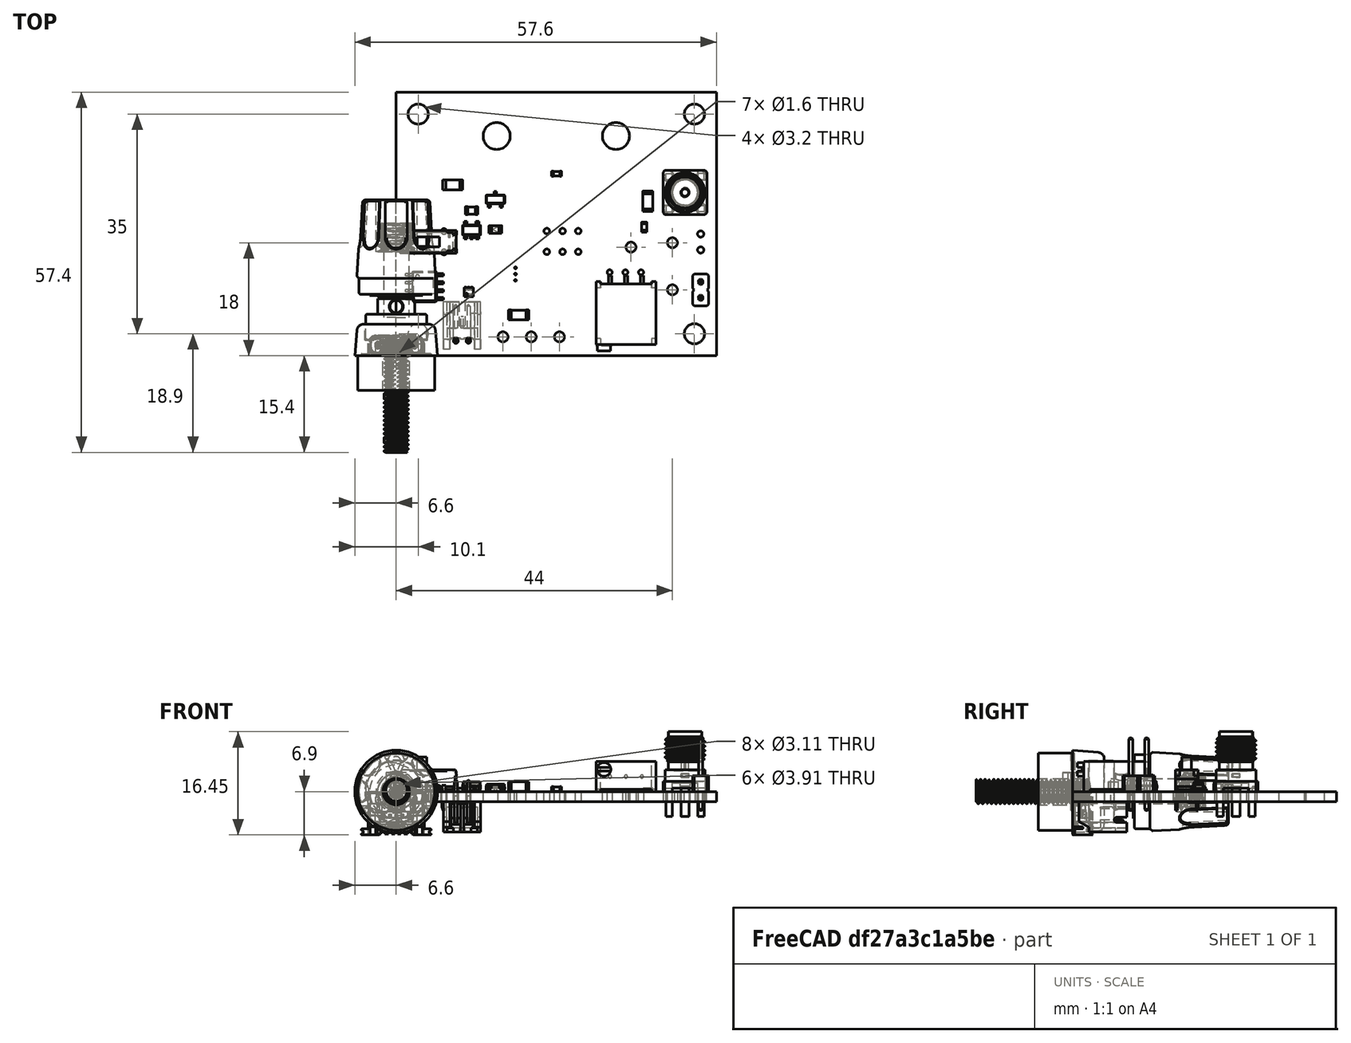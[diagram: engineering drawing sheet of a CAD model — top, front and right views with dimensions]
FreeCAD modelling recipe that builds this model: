
FCSTD DOCUMENT  (FreeCAD 0.20R29603 (Git))
Label: SCuSA_RevA1_PCBA
License: All rights reserved
LicenseURL: http://en.wikipedia.org/wiki/All_rights_reserved
objects: App::Link×51, Part::Feature×39, App::Part×12, PartDesign::CoordinateSystem×1, Sketcher::SketchObject×1
note: 41 computed .brp shape members not serialized (recipe doc carries the construction recipe); baked Part::Feature solids carry a one-line shape summary decoded from their .brp

FEATURE [PartDesign::CoordinateSystem] Local_CS_3e51
  AttacherType = Attacher::AttachEngine3D
  MapMode = 2
  Support = -> [X_Axis001]
FEATURE [Part::Feature] Pcb_3e51
  Placement = pos=(-112,104,0) rot=(0,0,1;0rad)
  shape: bbox 51 x 42 x 1.6 mm, 47 faces (baked)
FEATURE [Sketcher::SketchObject] PCB_Sketch_3e51
  FullyConstrained = false
  sketch-geometry (4):
    g0: LineSegment StartX=51 StartY=0 StartZ=0 EndX=0 EndY=0 EndZ=0
    g1: LineSegment StartX=0 StartY=42 StartZ=0 EndX=51 EndY=42 EndZ=0
    g2: LineSegment StartX=0 StartY=0 StartZ=0 EndX=0 EndY=42 EndZ=0
    g3: LineSegment StartX=51 StartY=42 StartZ=0 EndX=51 EndY=0 EndZ=0
  constraints (4):
    c: Coincident(g0,g2)
    c: Coincident(g1,g2)
    c: Coincident(g0,g3)
    c: Coincident(g1,g3)
FEATURE [App::Part] Board_Geoms_3e51
  Group = -> [Pcb_3e51,PCB_Sketch_3e51]
  Origin = -> Origin
FEATURE [Part::Feature] Shape  label="R118_R_1206_3216Metric_9a429e010c18"
  Placement = pos=(40.05,24.6,0) rot=(0,0,1;1.5708rad)
  shape: bbox 1.6 x 3.2 x 0.55 mm, 26 faces (baked)
FEATURE [Part::Feature] Shape001  label="C110_C_0603_1608Metric_07e89f88e059"
  Placement = pos=(25.55,29,0) rot=(0,0,1;3.14159rad)
  shape: bbox 1.6 x 0.8 x 0.8 mm, 28 faces (baked)
FEATURE [Part::Feature] Shape002  label="R121_R_0603_1608Metric_cabd63930a75"
  Placement = pos=(39.5,20.5,0) rot=(0,0,-1;1.5708rad)
  shape: bbox 0.8 x 1.6 x 0.45 mm, 26 faces (baked)
FEATURE [Part::Feature] Shape003  label="F101_Fuse_1206_3216Metric_160eb9ee9b08"
  Placement = pos=(9,27.2,0) rot=(0,0,1;0rad)
  shape: bbox 3.2 x 1.6 x 0.55 mm, 26 faces (baked)
FEATURE [Part::Feature] Shape004  label="J108_PinHeader_1x02_P254mm_Vertical_696c06d13264"
  Placement = pos=(48.5,9.225,0) rot=(0,0,1;3.14159rad)
  shape: bbox 2.54 x 5.08 x 11.54 mm, 52 faces (baked)
FEATURE [Part::Feature] Shape005  label="C101_C_0805_2012Metric_832099bd49ec"
  Placement = pos=(12,23.1,0) rot=(0,0,1;3.14159rad)
  shape: bbox 2 x 1.25 x 1.25 mm, 28 faces (baked)
FEATURE [App::Link] R121_R_0603_1608Metric_cabd63930a75_ln_  label="R103_R_0603_1608Metric_e52815511993"
  LinkPlacement = pos=(8.4,22.9,0) rot=(0,0,1;3.14159rad)
  LinkedObject = -> Shape002
  Placement = pos=(8.4,22.9,0) rot=(0,0,1;3.14159rad)
FEATURE [App::Link] C110_C_0603_1608Metric_07e89f88e059_ln_  label="C114_C_0603_1608Metric_c5f3be501f81"
  LinkPlacement = pos=(23.2,9.4,0) rot=(0,0,1;1.5708rad)
  LinkedObject = -> Shape001
  Placement = pos=(23.2,9.4,0) rot=(0,0,1;1.5708rad)
FEATURE [Part::Feature] Part__Feature  label="WSON-12 v7"
  shape: bbox 1 x 0.25 x 2.65 mm, 7 faces (baked)
FEATURE [Part::Feature] Part__Feature001  label="WSON-12 v008"
  shape: bbox 0.35 x 0.25 x 0.25 mm, 6 faces (baked)
FEATURE [Part::Feature] Part__Feature002  label="WSON-12 v009"
  shape: bbox 0.35 x 0.25 x 0.25 mm, 6 faces (baked)
FEATURE [Part::Feature] Part__Feature003  label="WSON-12 v010"
  shape: bbox 0.35 x 0.25 x 0.25 mm, 6 faces (baked)
FEATURE [Part::Feature] Part__Feature004  label="WSON-12 v011"
  shape: bbox 0.35 x 0.25 x 0.25 mm, 6 faces (baked)
FEATURE [Part::Feature] Part__Feature005  label="WSON-12 v012"
  shape: bbox 0.35 x 0.25 x 0.25 mm, 6 faces (baked)
FEATURE [Part::Feature] Part__Feature006  label="WSON-12 v013"
  shape: bbox 0.35 x 0.25 x 0.25 mm, 6 faces (baked)
FEATURE [Part::Feature] Part__Feature007  label="WSON-12 v014"
  shape: bbox 0.35 x 0.25 x 0.25 mm, 6 faces (baked)
FEATURE [Part::Feature] Part__Feature008  label="WSON-12 v015"
  shape: bbox 0.35 x 0.25 x 0.25 mm, 6 faces (baked)
FEATURE [Part::Feature] Part__Feature009  label="WSON-12 v016"
  shape: bbox 0.35 x 0.25 x 0.25 mm, 6 faces (baked)
FEATURE [Part::Feature] Part__Feature010  label="WSON-12 v017"
  shape: bbox 0.35 x 0.25 x 0.25 mm, 6 faces (baked)
FEATURE [Part::Feature] Part__Feature011  label="WSON-12 v018"
  shape: bbox 0.35 x 0.25 x 0.25 mm, 6 faces (baked)
FEATURE [Part::Feature] Part__Feature012  label="WSON-12 v019"
  shape: bbox 0.35 x 0.25 x 0.25 mm, 6 faces (baked)
FEATURE [Part::Feature] Part__Feature013  label="WSON-12 v020"
  shape: bbox 2.001 x 0.8006 x 3.001 mm, 603 faces (baked)
FEATURE [App::Part] WSON_12_v7  label="U104_WSON-12 v021_6ffd8b18686f"
  Group = -> [Part__Feature,Part__Feature001,Part__Feature002,Part__Feature003,Part__Feature004,Part__Feature005,Part__Feature006,Part__Feature007,Part__Feature008,Part__Feature009,Part__Feature010,Part__Feature011,Part__Feature012,Part__Feature013]
  Origin = -> Origin008
  Placement = pos=(19,13,0) rot=(1,0,0;1.5708rad)
FEATURE [Part::Feature] Part__Feature014  label="TestPoint_Loop_D2_60mm_Drill1_6mm_Beaded_cp"
  shape: bbox 3.2 x 3.2 x 3 mm, 4 faces (baked)
FEATURE [Part::Feature] Part__Feature015  label="TestPoint_Loop_D2_60mm_Drill1_6mm_Beaded_cp001"
  shape: bbox 3.649 x 1.14 x 9.307 mm, 7 faces (baked)
FEATURE [App::Part] TestPoint_Loop_D2_60mm_Drill1_6mm_Beaded_cp  label="TP106_TestPoint_Loop_D2_60mm_Drill1_6mm_Beaded_cp002_0780feeba4dd"
  Group = -> [Part__Feature014,Part__Feature015]
  Origin = -> Origin009
  Placement = pos=(37.4,17.3,0) rot=(0,0,1;1.5708rad)
FEATURE [App::Link] R121_R_0603_1608Metric_cabd63930a75_ln_001  label="R105_R_0603_1608Metric_8828eca0330c"
  LinkPlacement = pos=(12.2,13.75,0) rot=(0,0,1;3.14159rad)
  LinkedObject = -> Shape002
  Placement = pos=(12.2,13.75,0) rot=(0,0,1;3.14159rad)
FEATURE [App::Link] C101_C_0805_2012Metric_832099bd49ec_ln_  label="C102_C_0805_2012Metric_9881d72c0956"
  LinkPlacement = pos=(11.9,16.9,0) rot=(0,0,1;3.14159rad)
  LinkedObject = -> Shape005
  Placement = pos=(11.9,16.9,0) rot=(0,0,1;3.14159rad)
FEATURE [App::Link] C110_C_0603_1608Metric_07e89f88e059_ln_001  label="C111_C_0603_1608Metric_e0c0d5fa783b"
  LinkPlacement = pos=(22.2,29,0) rot=(0,0,1;3.14159rad)
  LinkedObject = -> Shape001
  Placement = pos=(22.2,29,0) rot=(0,0,1;3.14159rad)
FEATURE [App::Link] R121_R_0603_1608Metric_cabd63930a75_ln_002  label="R113_R_0603_1608Metric_61fe00350bf9"
  LinkPlacement = pos=(19.05,8.5,0) rot=(0,0,1;3.14159rad)
  LinkedObject = -> Shape002
  Placement = pos=(19.05,8.5,0) rot=(0,0,1;3.14159rad)
FEATURE [App::Link] C110_C_0603_1608Metric_07e89f88e059_ln_002  label="C106_C_0603_1608Metric_96d47e7760c2"
  LinkPlacement = pos=(21.55,13,0) rot=(0,0,-1;1.5708rad)
  LinkedObject = -> Shape001
  Placement = pos=(21.55,13,0) rot=(0,0,-1;1.5708rad)
FEATURE [App::Link] C110_C_0603_1608Metric_07e89f88e059_ln_003  label="C109_C_0603_1608Metric_a759c64c54e8"
  LinkPlacement = pos=(28.9,29,0) rot=(0,0,1;3.14159rad)
  LinkedObject = -> Shape001
  Placement = pos=(28.9,29,0) rot=(0,0,1;3.14159rad)
FEATURE [App::Link] C110_C_0603_1608Metric_07e89f88e059_ln_004  label="C115_C_0603_1608Metric_735d576579cb"
  LinkPlacement = pos=(28.9,22,0) rot=(0,0,1;0rad)
  LinkedObject = -> Shape001
  Placement = pos=(28.9,22,0) rot=(0,0,1;0rad)
FEATURE [App::Link] TP106_TestPoint_Loop_D2_60mm_Drill1_6mm_Beaded_cp002_0780feeba4dd_ln_  label="TP102_TestPoint_Loop_D2_60mm_Drill1_6mm_Beaded_cp002_ab26968e4f7d"
  LinkPlacement = pos=(17,3,0) rot=(0,0,1;0rad)
  LinkedObject = -> TestPoint_Loop_D2_60mm_Drill1_6mm_Beaded_cp
  Placement = pos=(17,3,0) rot=(0,0,1;0rad)
FEATURE [App::Link] C101_C_0805_2012Metric_832099bd49ec_ln_001  label="C108_C_0805_2012Metric_e86135985600"
  LinkPlacement = pos=(16,9.25,0) rot=(0,0,-1;1.5708rad)
  LinkedObject = -> Shape005
  Placement = pos=(16,9.25,0) rot=(0,0,-1;1.5708rad)
FEATURE [Part::Feature] Shape006  label="Q101_SOIC_8_39x49mm_P127mm_18785c1fbfb3"
  Placement = pos=(4.5,11,0) rot=(0,0,1;0rad)
  shape: bbox 6 x 4.9 x 1.75 mm, 156 faces (baked)
FEATURE [App::Link] R121_R_0603_1608Metric_cabd63930a75_ln_003  label="R109_R_0603_1608Metric_f4df95fcec91"
  LinkPlacement = pos=(15.8,22.15,0) rot=(0,0,1;0rad)
  LinkedObject = -> Shape002
  Placement = pos=(15.8,22.15,0) rot=(0,0,1;0rad)
FEATURE [Part::Feature] Shape007  label="SW101_CuK_JS202011CQN_DPDT_straight_5f730d750727"
  Placement = pos=(7.6075,16.5,0) rot=(0,0,1;3.14159rad)
  shape: bbox 9 x 3.61 x 8.5 mm, 178 faces (baked)
FEATURE [App::Link] C110_C_0603_1608Metric_07e89f88e059_ln_005  label="C118_C_0603_1608Metric_af693a659c10"
  LinkPlacement = pos=(33.2,20.1,0) rot=(0,0,1;0rad)
  LinkedObject = -> Shape001
  Placement = pos=(33.2,20.1,0) rot=(0,0,1;0rad)
FEATURE [App::Link] SW101_CuK_JS202011CQN_DPDT_straight_5f730d750727_ln_  label="SW102_CuK_JS202011CQN_DPDT_straight_acea3379d2f1"
  LinkPlacement = pos=(23.9925,19.85,0) rot=(0,0,1;0rad)
  LinkedObject = -> Shape007
  Placement = pos=(23.9925,19.85,0) rot=(0,0,1;0rad)
FEATURE [App::Link] C110_C_0603_1608Metric_07e89f88e059_ln_006  label="C105_C_0603_1608Metric_287e28563a33"
  LinkPlacement = pos=(20,15.7,0) rot=(0,0,1;3.14159rad)
  LinkedObject = -> Shape001
  Placement = pos=(20,15.7,0) rot=(0,0,1;3.14159rad)
FEATURE [App::Link] TP106_TestPoint_Loop_D2_60mm_Drill1_6mm_Beaded_cp002_0780feeba4dd_ln_001  label="TP101_TestPoint_Loop_D2_60mm_Drill1_6mm_Beaded_cp002_a418f8038e49"
  LinkPlacement = pos=(21.5,3,0) rot=(0,0,1;0rad)
  LinkedObject = -> TestPoint_Loop_D2_60mm_Drill1_6mm_Beaded_cp
  Placement = pos=(21.5,3,0) rot=(0,0,1;0rad)
FEATURE [Part::Feature] Shape008  label="FB101_L_1206_3216Metric_6ecc6a01b1a7"
  Placement = pos=(19.5,6.5,0) rot=(0,0,1;0rad)
  shape: bbox 3.2 x 1.6 x 1.6 mm, 28 faces (baked)
FEATURE [App::Link] C110_C_0603_1608Metric_07e89f88e059_ln_007  label="C117_C_0603_1608Metric_b9cc278da1dd"
  LinkPlacement = pos=(33.25,27.1,0) rot=(0,0,1;0rad)
  LinkedObject = -> Shape001
  Placement = pos=(33.25,27.1,0) rot=(0,0,1;0rad)
FEATURE [Part::Feature] Shape009  label="J105_60312002114503_f594866c6ba6"
  Placement = pos=(46,26,1.65) rot=(1,0,0;3.14159rad)
  shape: bbox 7.319 x 7.009 x 13.51 mm, 77 faces (baked)
FEATURE [App::Link] C110_C_0603_1608Metric_07e89f88e059_ln_008  label="C116_C_0603_1608Metric_dd78862adcb4"
  LinkPlacement = pos=(20.7,25.2,0) rot=(0,0,1;1.5708rad)
  LinkedObject = -> Shape001
  Placement = pos=(20.7,25.2,0) rot=(0,0,1;1.5708rad)
FEATURE [App::Link] C110_C_0603_1608Metric_07e89f88e059_ln_009  label="C104_C_0603_1608Metric_8d6246460c0c"
  LinkPlacement = pos=(16.5,13,0) rot=(0,0,-1;1.5708rad)
  LinkedObject = -> Shape001
  Placement = pos=(16.5,13,0) rot=(0,0,-1;1.5708rad)
FEATURE [App::Link] R121_R_0603_1608Metric_cabd63930a75_ln_004  label="R115_R_0603_1608Metric_e91c1c194d21"
  LinkPlacement = pos=(26.3,31.5,0) rot=(0,0,-1;1.5708rad)
  LinkedObject = -> Shape002
  Placement = pos=(26.3,31.5,0) rot=(0,0,-1;1.5708rad)
FEATURE [Part::Feature] Part__Feature016  label="USB4135-GF-A"
  shape: bbox 11.15 x 3.257 x 6.907 mm, 318 faces (baked)
FEATURE [Part::Feature] Part__Feature017  label="USB4135-GF-A001"
  shape: bbox 8.3 x 2.985 x 6.55 mm, 467 faces (baked)
FEATURE [App::Part] USB4135_GF_A  label="J101_USB4135-GF-A002_08b6693a03fd"
  Group = -> [Part__Feature016,Part__Feature017]
  Origin = -> Origin010
  Placement = pos=(-1.5175,29.25,0) rot=(0.57735,-0.57735,-0.57735;2.0944rad)
FEATURE [App::Link] FB101_L_1206_3216Metric_6ecc6a01b1a7_ln_  label="FB100_L_1206_3216Metric_5c9160750dc1"
  LinkPlacement = pos=(26.5,13.5,0) rot=(0,0,1;0rad)
  LinkedObject = -> Shape008
  Placement = pos=(26.5,13.5,0) rot=(0,0,1;0rad)
FEATURE [App::Link] R121_R_0603_1608Metric_cabd63930a75_ln_005  label="R112_R_0603_1608Metric_1715ab4cdc12"
  LinkPlacement = pos=(21.65,9.4,0) rot=(0,0,-1;1.5708rad)
  LinkedObject = -> Shape002
  Placement = pos=(21.65,9.4,0) rot=(0,0,-1;1.5708rad)
FEATURE [App::Link] TP106_TestPoint_Loop_D2_60mm_Drill1_6mm_Beaded_cp002_0780feeba4dd_ln_002  label="TP104_TestPoint_Loop_D2_60mm_Drill1_6mm_Beaded_cp002_50bb3ab2e26f"
  LinkPlacement = pos=(26,3,0) rot=(0,0,1;0rad)
  LinkedObject = -> TestPoint_Loop_D2_60mm_Drill1_6mm_Beaded_cp
  Placement = pos=(26,3,0) rot=(0,0,1;0rad)
FEATURE [App::Link] R118_R_1206_3216Metric_9a429e010c18_ln_  label="R114_R_1206_3216Metric_9449b8210d6c"
  LinkPlacement = pos=(25.5,34.35,0) rot=(0,0,1;3.14159rad)
  LinkedObject = -> Shape
  Placement = pos=(25.5,34.35,0) rot=(0,0,1;3.14159rad)
FEATURE [App::Link] C110_C_0603_1608Metric_07e89f88e059_ln_010  label="C107_C_0603_1608Metric_1132f46c80d0"
  LinkPlacement = pos=(19.05,10.25,0) rot=(0,0,1;0rad)
  LinkedObject = -> Shape001
  Placement = pos=(19.05,10.25,0) rot=(0,0,1;0rad)
FEATURE [App::Link] R121_R_0603_1608Metric_cabd63930a75_ln_006  label="R102_R_0603_1608Metric_428a7ca26184"
  LinkPlacement = pos=(8.2,29.15,0) rot=(0,0,1;0rad)
  LinkedObject = -> Shape002
  Placement = pos=(8.2,29.15,0) rot=(0,0,1;0rad)
FEATURE [App::Link] C110_C_0603_1608Metric_07e89f88e059_ln_011  label="C113_C_0603_1608Metric_c568501282b4"
  LinkPlacement = pos=(36.6,27.1,0) rot=(0,0,1;0rad)
  LinkedObject = -> Shape001
  Placement = pos=(36.6,27.1,0) rot=(0,0,1;0rad)
FEATURE [App::Link] R121_R_0603_1608Metric_cabd63930a75_ln_007  label="R116_R_0603_1608Metric_7018264d671d"
  LinkPlacement = pos=(24.8,31.5,0) rot=(0,0,-1;1.5708rad)
  LinkedObject = -> Shape002
  Placement = pos=(24.8,31.5,0) rot=(0,0,-1;1.5708rad)
FEATURE [Part::Feature] Shape010  label="D102_LED_0805_2012Metric_8af6430a5faa"
  Placement = pos=(15.8,20.1,0) rot=(0,0,1;0rad)
  shape: bbox 2 x 1.25 x 1.1 mm, 50 faces (baked)
FEATURE [App::Link] D102_LED_0805_2012Metric_8af6430a5faa_ln_  label="D103_LED_0805_2012Metric_5064c74abf3b"
  LinkPlacement = pos=(15.8,17.9,0) rot=(0,0,1;3.14159rad)
  LinkedObject = -> Shape010
  Placement = pos=(15.8,17.9,0) rot=(0,0,1;3.14159rad)
FEATURE [App::Link] C110_C_0603_1608Metric_07e89f88e059_ln_012  label="C112_C_0603_1608Metric_2f680c3bccde"
  LinkPlacement = pos=(25.55,22,0) rot=(0,0,1;3.14159rad)
  LinkedObject = -> Shape001
  Placement = pos=(25.55,22,0) rot=(0,0,1;3.14159rad)
FEATURE [App::Link] TP106_TestPoint_Loop_D2_60mm_Drill1_6mm_Beaded_cp002_0780feeba4dd_ln_003  label="TP108_TestPoint_Loop_D2_60mm_Drill1_6mm_Beaded_cp002_35738ac4b5fc"
  LinkPlacement = pos=(44,18,0) rot=(0,0,1;1.5708rad)
  LinkedObject = -> TestPoint_Loop_D2_60mm_Drill1_6mm_Beaded_cp
  Placement = pos=(44,18,0) rot=(0,0,1;1.5708rad)
FEATURE [App::Link] R121_R_0603_1608Metric_cabd63930a75_ln_008  label="R101_R_0603_1608Metric_6d1fb4459d4d"
  LinkPlacement = pos=(8.2,30.7,0) rot=(0,0,1;0rad)
  LinkedObject = -> Shape002
  Placement = pos=(8.2,30.7,0) rot=(0,0,1;0rad)
FEATURE [Part::Feature] Shape011  label="U103_SOT_23_415030393587"
  Placement = pos=(15.8,24.9,0) rot=(0,0,1;1.5708rad)
  shape: bbox 3 x 2.5 x 1.2 mm, 76 faces (baked)
FEATURE [App::Link] R121_R_0603_1608Metric_cabd63930a75_ln_009  label="R110_R_0603_1608Metric_f7e6a50cc7fa"
  LinkPlacement = pos=(20,17.25,0) rot=(0,0,1;3.14159rad)
  LinkedObject = -> Shape002
  Placement = pos=(20,17.25,0) rot=(0,0,1;3.14159rad)
FEATURE [App::Link] C110_C_0603_1608Metric_07e89f88e059_ln_013  label="C121_C_0603_1608Metric_b24aff25157a"
  LinkPlacement = pos=(41,20.5,0) rot=(0,0,1;1.5708rad)
  LinkedObject = -> Shape001
  Placement = pos=(41,20.5,0) rot=(0,0,1;1.5708rad)
FEATURE [App::Link] C110_C_0603_1608Metric_07e89f88e059_ln_014  label="C120_C_0603_1608Metric_3728ccd4f199"
  LinkPlacement = pos=(18.6,23.1375,0) rot=(0,0,1;1.5708rad)
  LinkedObject = -> Shape001
  Placement = pos=(18.6,23.1375,0) rot=(0,0,1;1.5708rad)
FEATURE [Part::Feature] Shape012  label="RV101_Cut_b268e7737479"
  Placement = pos=(41.55,22.79,6.4) rot=(0,0.707107,-0.707107;3.14159rad)
  shape: bbox 9.53 x 12.05 x 4.83 mm, 32 faces (baked)
FEATURE [App::Link] Q101_SOIC_8_39x49mm_P127mm_18785c1fbfb3_ln_  label="U105_SOIC_8_39x49mm_P127mm_81b4a2160633"
  LinkPlacement = pos=(25.55,25.5,0) rot=(0,0,1;0rad)
  LinkedObject = -> Shape006
  Placement = pos=(25.55,25.5,0) rot=(0,0,1;0rad)
FEATURE [App::Link] R121_R_0603_1608Metric_cabd63930a75_ln_010  label="R122_R_0603_1608Metric_47ff7c3b82b1"
  LinkPlacement = pos=(6.6,33.9125,0) rot=(0,0,-1;1.5708rad)
  LinkedObject = -> Shape002
  Placement = pos=(6.6,33.9125,0) rot=(0,0,-1;1.5708rad)
FEATURE [App::Link] C110_C_0603_1608Metric_07e89f88e059_ln_015  label="C103_C_0603_1608Metric_b43a54b29ec9"
  LinkPlacement = pos=(12.2,12.15,0) rot=(0,0,1;0rad)
  LinkedObject = -> Shape001
  Placement = pos=(12.2,12.15,0) rot=(0,0,1;0rad)
FEATURE [App::Link] R121_R_0603_1608Metric_cabd63930a75_ln_011  label="R104_R_0603_1608Metric_4504fa6f6234"
  LinkPlacement = pos=(12,24.9,0) rot=(0,0,1;3.14159rad)
  LinkedObject = -> Shape002
  Placement = pos=(12,24.9,0) rot=(0,0,1;3.14159rad)
FEATURE [App::Link] R121_R_0603_1608Metric_cabd63930a75_ln_012  label="R117_R_0603_1608Metric_145afd5d1bbc"
  LinkPlacement = pos=(15.75,16.05,0) rot=(0,0,1;3.14159rad)
  LinkedObject = -> Shape002
  Placement = pos=(15.75,16.05,0) rot=(0,0,1;3.14159rad)
FEATURE [App::Link] Q101_SOIC_8_39x49mm_P127mm_18785c1fbfb3_ln_001  label="U106_SOIC_8_39x49mm_P127mm_f8bf6cf0ab73"
  LinkPlacement = pos=(34.95,23.6,0) rot=(0,0,1;0rad)
  LinkedObject = -> Shape006
  Placement = pos=(34.95,23.6,0) rot=(0,0,1;0rad)
FEATURE [Part::Feature] Shape013  label="U101_SOT_23_5_b81ba866f2ca"
  Placement = pos=(12,20,0) rot=(0,0,1;1.5708rad)
  shape: bbox 2.9 x 2.8 x 1.55 mm, 109 faces (baked)
FEATURE [App::Link] R121_R_0603_1608Metric_cabd63930a75_ln_013  label="R108_R_0603_1608Metric_1a3b190c03d7"
  LinkPlacement = pos=(4.7,7.5,0) rot=(0,0,1;0rad)
  LinkedObject = -> Shape002
  Placement = pos=(4.7,7.5,0) rot=(0,0,1;0rad)
FEATURE [App::Link] R121_R_0603_1608Metric_cabd63930a75_ln_014  label="R111_R_0603_1608Metric_a0045bdc3730"
  LinkPlacement = pos=(20,18.8,0) rot=(0,0,1;0rad)
  LinkedObject = -> Shape002
  Placement = pos=(20,18.8,0) rot=(0,0,1;0rad)
FEATURE [Part::Feature] Shape014  label="U102_WSON6_15x15mm_Pitch05mm_e3a42ca1607c"
  Placement = pos=(11.55,10.15,0) rot=(0,0,1;1.5708rad)
  shape: bbox 1.48 x 1.5 x 0.77 mm, 44 faces (baked)
FEATURE [Part::Feature] Part__Feature018  label="Fusion"
  shape: bbox 13.53 x 40.44 x 13.53 mm, 185 faces (baked)
FEATURE [Part::Feature] Part__Feature019  label="Fusion001"
  shape: bbox 13.52 x 10.5 x 13.52 mm, 10 faces (baked)
FEATURE [App::Part] Fusion  label="J103_Fusion002_9d3f900d180c"
  Group = -> [Part__Feature018,Part__Feature019]
  Origin = -> Origin011
  Placement = pos=(35,35,5.5) rot=(0.57735,-0.57735,-0.57735;2.0944rad)
FEATURE [App::Link] D102_LED_0805_2012Metric_8af6430a5faa_ln_001  label="D101_LED_0805_2012Metric_902e5ca3932e"
  LinkPlacement = pos=(8.4,25,0) rot=(0,0,1;0rad)
  LinkedObject = -> Shape010
  Placement = pos=(8.4,25,0) rot=(0,0,1;0rad)
FEATURE [App::Link] J108_PinHeader_1x02_P254mm_Vertical_696c06d13264_ln_  label="J107_PinHeader_1x02_P254mm_Vertical_b8f4a2ff9044"
  LinkPlacement = pos=(48.5,16.845,0) rot=(0,0,1;3.14159rad)
  LinkedObject = -> Shape004
  Placement = pos=(48.5,16.845,0) rot=(0,0,1;3.14159rad)
FEATURE [App::Link] C110_C_0603_1608Metric_07e89f88e059_ln_016  label="C119_C_0603_1608Metric_dbd71c4523cc"
  LinkPlacement = pos=(29.75,12.5,0) rot=(0,0,-1;1.5708rad)
  LinkedObject = -> Shape001
  Placement = pos=(29.75,12.5,0) rot=(0,0,-1;1.5708rad)
FEATURE [App::Link] R121_R_0603_1608Metric_cabd63930a75_ln_015  label="R106_R_0603_1608Metric_9dcb38f3090e"
  LinkPlacement = pos=(9.6,11.8,0) rot=(0,0,1;1.5708rad)
  LinkedObject = -> Shape002
  Placement = pos=(9.6,11.8,0) rot=(0,0,1;1.5708rad)
FEATURE [App::Link] R121_R_0603_1608Metric_cabd63930a75_ln_016  label="R120_R_0603_1608Metric_a775436f9ad3"
  LinkPlacement = pos=(20,20.35,0) rot=(0,0,1;3.14159rad)
  LinkedObject = -> Shape002
  Placement = pos=(20,20.35,0) rot=(0,0,1;3.14159rad)
FEATURE [App::Link] TP106_TestPoint_Loop_D2_60mm_Drill1_6mm_Beaded_cp002_0780feeba4dd_ln_004  label="TP107_TestPoint_Loop_D2_60mm_Drill1_6mm_Beaded_cp002_804a37e84f20"
  LinkPlacement = pos=(44,10.5,0) rot=(0,0,1;1.5708rad)
  LinkedObject = -> TestPoint_Loop_D2_60mm_Drill1_6mm_Beaded_cp
  Placement = pos=(44,10.5,0) rot=(0,0,1;1.5708rad)
FEATURE [App::Link] R121_R_0603_1608Metric_cabd63930a75_ln_017  label="R107_R_0603_1608Metric_02283ed4e356"
  LinkPlacement = pos=(4.7,14.5,0) rot=(0,0,1;3.14159rad)
  LinkedObject = -> Shape002
  Placement = pos=(4.7,14.5,0) rot=(0,0,1;3.14159rad)
FEATURE [App::Link] R121_R_0603_1608Metric_cabd63930a75_ln_018  label="R119_R_0603_1608Metric_d680dbf24c9f"
  LinkPlacement = pos=(23.1,13,0) rot=(0,0,-1;1.5708rad)
  LinkedObject = -> Shape002
  Placement = pos=(23.1,13,0) rot=(0,0,-1;1.5708rad)
FEATURE [App::Part] Top_3e51
  Group = -> [Shape,Shape001,Shape002,Shape003,Shape004,Shape005,R121_R_0603_1608Metric_cabd63930a75_ln_,C110_C_0603_1608Metric_07e89f88e059_ln_,WSON_12_v7,TestPoint_Loop_D2_60mm_Drill1_6mm_Beaded_cp,R121_R_0603_1608Metric_cabd63930a75_ln_001,C101_C_0805_2012Metric_832099bd49ec_ln_,C110_C_0603_1608Metric_07e89f88e059_ln_001,R121_R_0603_1608Metric_cabd63930a75_ln_002,C110_C_0603_1608Metric_07e89f88e059_ln_002,+54 more]
  Origin = -> Origin003
FEATURE [Part::Feature] Part__Feature020  label="Fusion002"
  shape: bbox 13.53 x 40.44 x 13.53 mm, 185 faces (baked)
FEATURE [Part::Feature] Part__Feature021  label="Fusion003"
  shape: bbox 13.52 x 10.5 x 13.52 mm, 10 faces (baked)
FEATURE [App::Part] Fusion001  label="J104_Fusion004_39d20d171dee"
  Group = -> [Part__Feature020,Part__Feature021]
  Origin = -> Origin012
  Placement = pos=(16,35,5.5) rot=(0.57735,-0.57735,-0.57735;2.0944rad)
FEATURE [App::Part] TopV_3e51
  Group = -> [Fusion,Fusion001]
  Origin = -> Origin006
FEATURE [App::Part] Step_Virtual_Models_3e51
  Group = -> [TopV_3e51]
  Origin = -> Origin005
FEATURE [Part::Feature] Shape015  label="J102_JST_S2B_PH_K_64e658e90b66"
  Placement = pos=(9.5,2.35,-1.6) rot=(1,0,0;3.14159rad)
  shape: bbox 5.9 x 7.6 x 8.25 mm, 110 faces (baked)
FEATURE [App::Part] Bot_3e51
  Group = -> [Shape015]
  Origin = -> Origin004
FEATURE [App::Part] Step_Models_3e51
  Group = -> [Top_3e51,Bot_3e51]
  Origin = -> Origin002
FEATURE [App::Part] Board_3e51  label="SCuSA_PCBA"
  Group = -> [Local_CS_3e51,Board_Geoms_3e51,Step_Models_3e51,Step_Virtual_Models_3e51]
  Origin = -> Origin001
